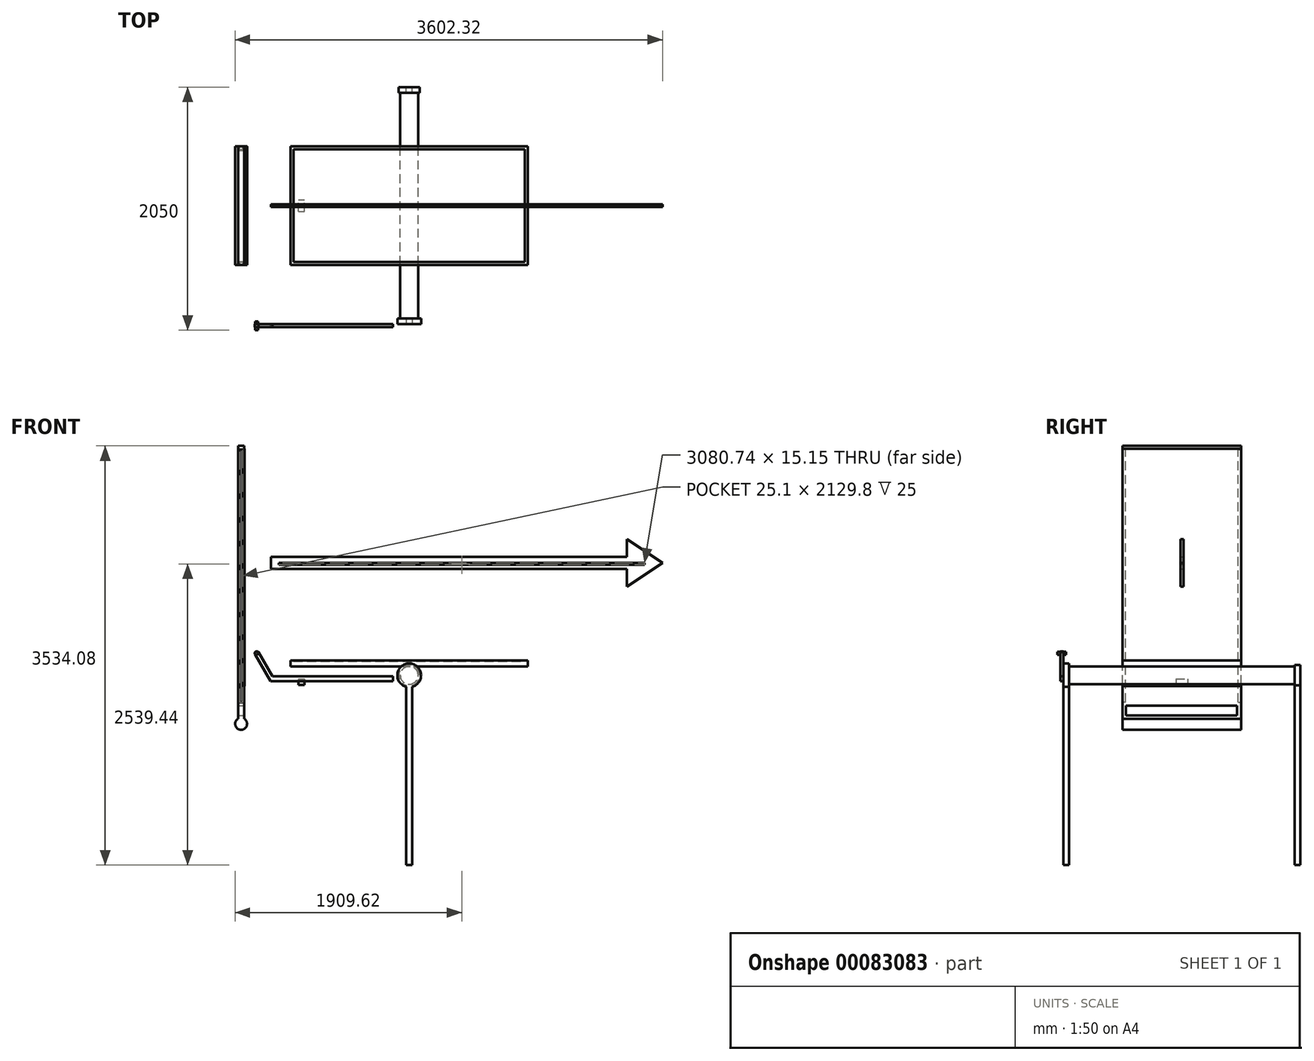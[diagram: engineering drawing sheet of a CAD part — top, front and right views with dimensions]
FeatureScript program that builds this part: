
annotation { "Feature Type Name" : "Feature", "Feature Type Description" : "" }
export const myFeature = defineFeature(function(context is Context, id is Id, definition is map)
    precondition{}
    {
        {
            var Q0;
            Q0=qCreatedBy(makeId("Top.planeOp"),FACE);
            var sketch = newSketch(context, id + "F0", { "sketchPlane" : qUnion([Q0])});
            skLineSegment(sketch, "E0.bottom", {"start": v(-1000, 500) * mm, "end": v(1000, 500) * mm});
            skLineSegment(sketch, "E0.top", {"start": v(-1000, -500) * mm, "end": v(1000, -500) * mm});
            skLineSegment(sketch, "E0.left", {"start": v(-1000, 500) * mm, "end": v(-1000, -500) * mm});
            skLineSegment(sketch, "E0.right", {"start": v(1000, 500) * mm, "end": v(1000, -500) * mm});
            skLineSegment(sketch, "E1", {"start": v(-1000, -500) * mm, "end": v(1000, 500) * mm, "construction": true});
            skSolve(sketch);
        }
        {
            var Q0;
            Q0=makeQuery(id+"F0.imprint","IMPRINT",FACE,{"disambiguationData":[TD([[makeQuery(id+"F0.imprint","IMPRINT",EDGE,{"derivedFrom":sQuery(id+"F0.wireOp",EDGE,"E0.bottom")}),-1.0]])]});
            extrude(context, id + "F1", {"entities" : qUnion([Q0]), "endBound" : BoundingType.SYMMETRIC, "depth" : 50 * mm});
        }
        {
            var Q0;
            Q0=makeQuery(id+"F1.opExtrude","CAP_FACE",FACE,{"disambiguationData":[OSD([sQuery(id+"F0.wireOp",EDGE,"E0.bottom"),sQuery(id+"F0.wireOp",EDGE,"E0.top"),sQuery(id+"F0.wireOp",EDGE,"E0.left"),sQuery(id+"F0.wireOp",EDGE,"E0.right")])],"isStart":false});
            var sketch = newSketch(context, id + "F2", { "sketchPlane" : qUnion([Q0])});
            skLineSegment(sketch, "E2.0", {"start": v(-1000, 500) * mm, "end": v(1000, 500) * mm});
            skLineSegment(sketch, "E3.0", {"start": v(-1000, 500) * mm, "end": v(-1000, -500) * mm});
            skLineSegment(sketch, "E4.0", {"start": v(-1000, -500) * mm, "end": v(1000, -500) * mm});
            skLineSegment(sketch, "E5.0", {"start": v(1000, 500) * mm, "end": v(1000, -500) * mm});
            skLineSegment(sketch, "E6.0", {"start": v(975, 475) * mm, "end": v(975, -475) * mm});
            skLineSegment(sketch, "E6.1", {"start": v(-975, 475) * mm, "end": v(975, 475) * mm});
            skLineSegment(sketch, "E6.2", {"start": v(-975, 475) * mm, "end": v(-975, -475) * mm});
            skLineSegment(sketch, "E6.3", {"start": v(-975, -475) * mm, "end": v(975, -475) * mm});
            skSolve(sketch);
        }
        {
            var Q0;
            Q0=makeQuery(id+"F2.imprint","IMPRINT",FACE,{"disambiguationData":[TD([[makeQuery(id+"F2.imprint","IMPRINT",EDGE,{"derivedFrom":sQuery(id+"F2.wireOp",EDGE,"E2.0")}),-1.0]])]});
            var sketch = newSketch(context, id + "F3", { "sketchPlane" : qUnion([Q0])});
            skSolve(sketch);
        }
        {
            var Q0;
            Q0 = qSketchRegion(id + "F3", true);
            var Q1;
            Q1=makeQuery(id+"F2.imprint","IMPRINT",FACE,{"disambiguationData":[TD([[makeQuery(id+"F2.imprint","IMPRINT",EDGE,{"derivedFrom":sQuery(id+"F2.wireOp",EDGE,"E6.0")}),-1.0]])]});
            extrude(context, id + "F4", {"entities" : qUnion([Q0, Q1]), "operationType" : NewBodyOperationType.REMOVE, "oppositeDirection" : true, "depth" : 5 * mm});
        }
        {
            var Q0;
            Q0=qCreatedBy(makeId("Front.planeOp"),FACE);
            var sketch = newSketch(context, id + "F5", { "sketchPlane" : qUnion([Q0])});
            skCircle(sketch, "E7", {"center": v(0, -100) * mm, "radius": 75 * mm});
            skSolve(sketch);
        }
        {
            var Q0;
            Q0 = qSketchRegion(id + "F5", true);
            extrude(context, id + "F6", {"entities" : qUnion([Q0]), "operationType" : NewBodyOperationType.ADD, "endBound" : BoundingType.SYMMETRIC, "depth" : 2000 * mm});
        }
        {
            var Q0;
            Q0=makeQuery(id+"F6.opExtrude","CAP_FACE",FACE,{"disambiguationData":[OSD([sQuery(id+"F5.wireOp",EDGE,"E7")])],"isStart":false});
            var sketch = newSketch(context, id + "F7", { "sketchPlane" : qUnion([Q0])});
            skCircle(sketch, "E8.0", {"center": v(0, -100) * mm, "radius": 75 * mm});
            skCircle(sketch, "E9", {"center": v(0, -100) * mm, "radius": 100 * mm});
            skSolve(sketch);
        }
        {
            var Q0;
            Q0 = qSketchRegion(id + "F7", true);
            extrude(context, id + "F8", {"entities" : qUnion([Q0]), "operationType" : NewBodyOperationType.ADD, "oppositeDirection" : true, "depth" : 50 * mm});
        }
        {
            var Q0;
            Q0=makeQuery(id+"F8.boolean.opBoolean","MERGE",FACE,{"derivedFrom":[makeQuery(id+"F6.opExtrude","CAP_FACE",FACE,{"disambiguationData":[OSD([sQuery(id+"F5.wireOp",EDGE,"E7")])],"isStart":false}),makeQuery(id+"F8.opExtrude","CAP_FACE",FACE,{"disambiguationData":[OSD([sQuery(id+"F7.wireOp",EDGE,"E8.0"),sQuery(id+"F7.wireOp",EDGE,"E9")])],"isStart":true})]});
            var sketch = newSketch(context, id + "F9", { "sketchPlane" : qUnion([Q0])});
            skLineSegment(sketch, "E10.bottom", {"start": v(-25, -100) * mm, "end": v(25, -100) * mm});
            skLineSegment(sketch, "E10.top", {"start": v(-25, -1700) * mm, "end": v(25, -1700) * mm});
            skLineSegment(sketch, "E10.left", {"start": v(-25, -100) * mm, "end": v(-25, -1700) * mm});
            skLineSegment(sketch, "E10.right", {"start": v(25, -100) * mm, "end": v(25, -1700) * mm});
            skPoint(sketch, "E11", {"position": v(0, -100) * mm});
            skSolve(sketch);
        }
        {
            var Q0;
            Q0 = qSketchRegion(id + "F9", true);
            extrude(context, id + "F10", {"entities" : qUnion([Q0]), "operationType" : NewBodyOperationType.ADD, "oppositeDirection" : true, "depth" : 50 * mm});
        }
        {
            var Q0;
            Q0=makeQuery(id+"F6.opExtrude","CAP_FACE",FACE,{"disambiguationData":[OSD([sQuery(id+"F5.wireOp",EDGE,"E7")])],"isStart":true});
            var sketch = newSketch(context, id + "F11", { "sketchPlane" : qUnion([Q0])});
            skCircle(sketch, "E12", {"center": v(0, -100) * mm, "radius": 87.5 * mm});
            skCircle(sketch, "E13.0", {"center": v(0, -100) * mm, "radius": 75 * mm});
            skSolve(sketch);
        }
        {
            var Q0;
            Q0 = qSketchRegion(id + "F11", true);
            extrude(context, id + "F12", {"entities" : qUnion([Q0]), "operationType" : NewBodyOperationType.ADD, "oppositeDirection" : true, "depth" : 50 * mm});
        }
        {
            var Q0;
            Q0=makeQuery(id+"F12.boolean.opBoolean","MERGE",FACE,{"derivedFrom":[makeQuery(id+"F6.opExtrude","CAP_FACE",FACE,{"disambiguationData":[OSD([sQuery(id+"F5.wireOp",EDGE,"E7")])],"isStart":true}),makeQuery(id+"F12.opExtrude","CAP_FACE",FACE,{"disambiguationData":[OSD([sQuery(id+"F11.wireOp",EDGE,"E12"),sQuery(id+"F11.wireOp",EDGE,"E13.0")])],"isStart":true})]});
            var sketch = newSketch(context, id + "F13", { "sketchPlane" : qUnion([Q0])});
            skLineSegment(sketch, "E14.0", {"start": v(25, -100) * mm, "end": v(-25, -100) * mm});
            skLineSegment(sketch, "E14.1", {"start": v(25, -1700) * mm, "end": v(-25, -1700) * mm});
            skLineSegment(sketch, "E14.2", {"start": v(25, -100) * mm, "end": v(25, -1700) * mm});
            skLineSegment(sketch, "E14.3", {"start": v(-25, -100) * mm, "end": v(-25, -1700) * mm});
            skPoint(sketch, "E14.4", {"position": v(0, -100) * mm});
            skSolve(sketch);
        }
        {
            var Q0;
            Q0 = qSketchRegion(id + "F13", true);
            extrude(context, id + "F14", {"entities" : qUnion([Q0]), "operationType" : NewBodyOperationType.ADD, "oppositeDirection" : true, "depth" : 50 * mm});
        }
        {
            var Q0;
            Q0=qCreatedBy(makeId("Front.planeOp"),FACE);
            var sketch = newSketch(context, id + "F15", { "sketchPlane" : qUnion([Q0])});
            skArc(sketch, "E15", {"start": v(-1441.7, -465.92) * mm, "mid": v(-1416.7, -559.22) * mm, "end": v(-1391.7, -465.92) * mm});
            skLineSegment(sketch, "E16.top", {"start": v(-1441.7, 1834.08) * mm, "end": v(-1391.7, 1834.08) * mm});
            skLineSegment(sketch, "E16.left", {"start": v(-1441.7, -465.92) * mm, "end": v(-1441.7, 1834.08) * mm});
            skLineSegment(sketch, "E16.right", {"start": v(-1391.7, -465.92) * mm, "end": v(-1391.7, 1834.08) * mm});
            skSolve(sketch);
        }
        {
            var Q0;
            Q0 = qSketchRegion(id + "F15", true);
            extrude(context, id + "F16", {"entities" : qUnion([Q0]), "endBound" : BoundingType.SYMMETRIC, "depth" : 1000 * mm});
        }
        {
            var Q0;
            Q0=makeQuery(id+"F16.opExtrude","CAP_FACE",FACE,{"disambiguationData":[OSD([sQuery(id+"F15.wireOp",EDGE,"E15"),sQuery(id+"F15.wireOp",EDGE,"E16.top"),sQuery(id+"F15.wireOp",EDGE,"E16.left"),sQuery(id+"F15.wireOp",EDGE,"E16.right")])],"isStart":false});
            var sketch = newSketch(context, id + "F17", { "sketchPlane" : qUnion([Q0])});
            skLineSegment(sketch, "E17.bottom", {"start": v(-1429.3, -326.34) * mm, "end": v(-1404.2, -326.34) * mm});
            skLineSegment(sketch, "E17.left", {"start": v(-1429.3, -326.34) * mm, "end": v(-1429.3, 1803.46) * mm});
            skLineSegment(sketch, "E17.right", {"start": v(-1404.2, -326.34) * mm, "end": v(-1404.2, 1803.46) * mm});
            skLineSegment(sketch, "E18", {"start": v(-1429.3, 1803.46) * mm, "end": v(-1404.2, 1803.46) * mm});
            skSolve(sketch);
        }
        {
            var Q0;
            Q0 = qSketchRegion(id + "F17", true);
            extrude(context, id + "F18", {"entities" : qUnion([Q0]), "operationType" : NewBodyOperationType.REMOVE, "oppositeDirection" : true, "depth" : 25 * mm});
        }
        {
            var Q0;
            Q0=makeQuery(id+"F16.opExtrude","SWEPT_BODY",BODY,{"disambiguationData":[OSD([sQuery(id+"F15.wireOp",EDGE,"E15"),sQuery(id+"F15.wireOp",EDGE,"E16.top"),sQuery(id+"F15.wireOp",EDGE,"E16.left"),sQuery(id+"F15.wireOp",EDGE,"E16.right")])]});
            var Q1;
            Q1=makeQuery(id+"F18.boolean.opBoolean","COPY",FACE,{"derivedFrom":makeQuery(id+"F18.opExtrude","SWEPT_FACE",FACE,{"disambiguationData":[OSD([sQuery(id+"F17.wireOp",EDGE,"E17.bottom")])]})});
            var Q2;
            Q2=makeQuery(id+"F18.boolean.opBoolean","COPY",FACE,{"derivedFrom":makeQuery(id+"F18.opExtrude","CAP_FACE",FACE,{"disambiguationData":[OSD([sQuery(id+"F17.wireOp",EDGE,"E17.bottom"),sQuery(id+"F17.wireOp",EDGE,"E17.left"),sQuery(id+"F17.wireOp",EDGE,"E17.right"),sQuery(id+"F17.wireOp",EDGE,"E18")])],"isStart":false})});
            var Q3;
            Q3=makeQuery(id+"F18.boolean.opBoolean","COPY",FACE,{"derivedFrom":makeQuery(id+"F18.opExtrude","SWEPT_FACE",FACE,{"disambiguationData":[OSD([sQuery(id+"F17.wireOp",EDGE,"E17.left")])]})});
            var Q4;
            Q4=makeQuery(id+"F18.boolean.opBoolean","COPY",FACE,{"derivedFrom":makeQuery(id+"F18.opExtrude","SWEPT_FACE",FACE,{"disambiguationData":[OSD([sQuery(id+"F17.wireOp",EDGE,"E17.right")])]})});
            var Q5;
            Q5=makeQuery(id+"F18.boolean.opBoolean","COPY",FACE,{"derivedFrom":makeQuery(id+"F18.opExtrude","SWEPT_FACE",FACE,{"disambiguationData":[OSD([sQuery(id+"F17.wireOp",EDGE,"E18")])]})});
            var Q6;
            Q6=qCreatedBy(makeId("Front.planeOp"),FACE);
            mirror(context, id + "F19", {"entities" : qUnion([Q0]), "faces" : qUnion([Q1, Q2, Q3, Q4, Q5]), "mirrorPlane" : qUnion([Q6]), "patternType" : MirrorType.FACE});
        }
        {
            var Q0;
            Q0=makeQuery(id+"F16.opExtrude","SWEPT_FACE",FACE,{"disambiguationData":[OSD([sQuery(id+"F15.wireOp",EDGE,"E16.right")])]});
            var sketch = newSketch(context, id + "F20", { "sketchPlane" : qUnion([Q0])});
            skLineSegment(sketch, "E19.bottom", {"start": v(-470.62, -438.51) * mm, "end": v(465.7, -438.51) * mm});
            skLineSegment(sketch, "E19.top", {"start": v(-470.62, -355.39) * mm, "end": v(465.7, -355.39) * mm});
            skLineSegment(sketch, "E19.left", {"start": v(-470.62, -438.51) * mm, "end": v(-470.62, -355.39) * mm});
            skLineSegment(sketch, "E19.right", {"start": v(465.7, -438.51) * mm, "end": v(465.7, -355.39) * mm});
            skSolve(sketch);
        }
        {
            var Q0;
            Q0 = qSketchRegion(id + "F20", true);
            extrude(context, id + "F21", {"entities" : qUnion([Q0]), "operationType" : NewBodyOperationType.REMOVE, "endBound" : BoundingType.THROUGH_ALL, "oppositeDirection" : true, "depth" : 25 * mm});
        }
        {
            var Q0;
            Q0=makeQuery(id+"F16.opExtrude","SWEPT_FACE",FACE,{"disambiguationData":[OSD([sQuery(id+"F15.wireOp",EDGE,"E16.right")])]});
            var sketch = newSketch(context, id + "F22", { "sketchPlane" : qUnion([Q0])});
            skLineSegment(sketch, "E20.bottom", {"start": v(-500, 1809.08) * mm, "end": v(500, 1809.08) * mm});
            skLineSegment(sketch, "E20.top", {"start": v(-500, -190.92) * mm, "end": v(500, -190.92) * mm});
            skLineSegment(sketch, "E20.left", {"start": v(-500, 1809.08) * mm, "end": v(-500, -190.92) * mm});
            skLineSegment(sketch, "E20.right", {"start": v(500, 1809.08) * mm, "end": v(500, -190.92) * mm});
            skSolve(sketch);
        }
        {
            var Q0;
            Q0 = qSketchRegion(id + "F22", true);
            extrude(context, id + "F23", {"entities" : qUnion([Q0]), "operationType" : NewBodyOperationType.ADD, "depth" : 4 * mm});
        }
        {
            var Q0;
            Q0=makeQuery(id+"F7.imprint","IMPRINT",FACE,{"disambiguationData":[TD([[makeQuery(id+"F7.imprint","IMPRINT",EDGE,{"derivedFrom":sQuery(id+"F7.wireOp",EDGE,"E8.0")}),1.0]])]});
            var sketch = newSketch(context, id + "F24", { "sketchPlane" : qUnion([Q0])});
            skLineSegment(sketch, "E21", {"start": v(-136.39, -109.44) * mm, "end": v(-1152.42, -109.44) * mm});
            skLineSegment(sketch, "E22", {"start": v(-1152.42, -109.44) * mm, "end": v(-1270.64, 95.33) * mm});
            skLineSegment(sketch, "E23", {"start": v(-1300.02, 76.23) * mm, "end": v(-1169.74, -149.44) * mm});
            skLineSegment(sketch, "E24", {"start": v(-1169.74, -149.44) * mm, "end": v(-136.39, -149.44) * mm});
            skLineSegment(sketch, "E25", {"start": v(-136.39, -109.44) * mm, "end": v(-136.39, -149.44) * mm});
            skCircle(sketch, "E26", {"center": v(-1284.83, 85) * mm, "radius": 12.5 * mm});
            skArc(sketch, "E27", {"start": v(-1270.64, 95.33) * mm, "mid": v(-1294.4, 99.71) * mm, "end": v(-1300.02, 76.23) * mm});
            skSolve(sketch);
        }
        {
            var Q0;
            Q0 = qSketchRegion(id + "F24", true);
            var Q1;
            Q1 = qSketchRegion(id + "F26", true);
            extrude(context, id + "F25", {"entities" : qUnion([Q0, Q1]), "depth" : 25 * mm});
        }
        {
            var Q0;
            Q0=makeQuery(id+"F25.opExtrude","CAP_FACE",FACE,{"disambiguationData":[OSD([sQuery(id+"F24.wireOp",EDGE,"E21"),sQuery(id+"F24.wireOp",EDGE,"E22"),sQuery(id+"F24.wireOp",EDGE,"E23"),sQuery(id+"F24.wireOp",EDGE,"E24"),sQuery(id+"F24.wireOp",EDGE,"E25"),sQuery(id+"F24.wireOp",EDGE,"E26"),sQuery(id+"F24.wireOp",EDGE,"E27")])],"isStart":false});
            var sketch = newSketch(context, id + "F26", { "sketchPlane" : qUnion([Q0])});
            skCircle(sketch, "E28.0", {"center": v(-1284.83, 85) * mm, "radius": 12.5 * mm});
            skSolve(sketch);
        }
        {
            var Q0;
            Q0 = qSketchRegion(id + "F26", true);
            extrude(context, id + "F27", {"entities" : qUnion([Q0]), "operationType" : NewBodyOperationType.ADD, "oppositeDirection" : true, "depth" : 50 * mm, "hasSecondDirection" : true, "secondDirectionOppositeDirection" : false, "secondDirectionDepth" : 25 * mm});
        }
        {
            var Q0;
            Q0=qCreatedBy(makeId("Front.planeOp"),FACE);
            var sketch = newSketch(context, id + "F28", { "sketchPlane" : qUnion([Q0])});
            skLineSegment(sketch, "E29", {"start": v(-1164.4, 797.02) * mm, "end": v(1835.6, 797.02) * mm});
            skLineSegment(sketch, "E30", {"start": v(1835.6, 797.02) * mm, "end": v(1835.6, 647.02) * mm});
            skLineSegment(sketch, "E31", {"start": v(1835.6, 647.02) * mm, "end": v(2135.6, 847.02) * mm});
            skLineSegment(sketch, "E32", {"start": v(2135.6, 847.02) * mm, "end": v(1835.6, 1047.02) * mm});
            skLineSegment(sketch, "E33", {"start": v(1835.6, 1047.02) * mm, "end": v(1835.6, 897.02) * mm});
            skLineSegment(sketch, "E34", {"start": v(1835.6, 897.02) * mm, "end": v(-1164.4, 897.02) * mm});
            skLineSegment(sketch, "E35", {"start": v(-1164.4, 897.02) * mm, "end": v(-1164.4, 797.02) * mm});
            skSolve(sketch);
        }
        {
            var Q0;
            Q0 = qSketchRegion(id + "F28", true);
            extrude(context, id + "F29", {"entities" : qUnion([Q0]), "operationType" : NewBodyOperationType.ADD, "endBound" : BoundingType.SYMMETRIC, "depth" : 25 * mm});
        }
        {
            var Q0;
            Q0=makeQuery(id+"F29.opExtrude","CAP_EDGE",EDGE,{"disambiguationData":[OSD([sQuery(id+"F28.wireOp",EDGE,"E35")])],"isStart":false});
            cPlane(context, id + "F30", {"entities" : qUnion([Q0]), "cplaneType" : CPlaneType.MID_PLANE, "offset" : 150 * mm, "width" : 150 * mm, "height" : 150 * mm});
        }
        {
            var Q0;
            Q0=makeQuery(id+"F29.opExtrude","CAP_FACE",FACE,{"disambiguationData":[OSD([sQuery(id+"F28.wireOp",EDGE,"E29"),sQuery(id+"F28.wireOp",EDGE,"E30"),sQuery(id+"F28.wireOp",EDGE,"E31"),sQuery(id+"F28.wireOp",EDGE,"E32"),sQuery(id+"F28.wireOp",EDGE,"E33"),sQuery(id+"F28.wireOp",EDGE,"E34"),sQuery(id+"F28.wireOp",EDGE,"E35")])],"isStart":false});
            var sketch = newSketch(context, id + "F31", { "sketchPlane" : qUnion([Q0])});
            skLineSegment(sketch, "E36.bottom", {"start": v(1983.28, 847.02) * mm, "end": v(-1097.46, 847.02) * mm});
            skLineSegment(sketch, "E36.top", {"start": v(1983.28, 831.87) * mm, "end": v(-1097.46, 831.87) * mm});
            skLineSegment(sketch, "E36.left", {"start": v(1983.28, 847.02) * mm, "end": v(1983.28, 831.87) * mm});
            skLineSegment(sketch, "E36.right", {"start": v(-1097.46, 847.02) * mm, "end": v(-1097.46, 831.87) * mm});
            skSolve(sketch);
        }
        {
            var Q0;
            Q0 = qSketchRegion(id + "F31", true);
            extrude(context, id + "F32", {"entities" : qUnion([Q0]), "operationType" : NewBodyOperationType.REMOVE, "endBound" : BoundingType.THROUGH_ALL, "oppositeDirection" : true, "depth" : 25 * mm});
        }
        {
            var Q0;
            Q0=qCreatedBy(makeId("Front.planeOp"),FACE);
            var sketch = newSketch(context, id + "F33", { "sketchPlane" : qUnion([Q0])});
            skCircle(sketch, "E37", {"center": v(-900.5, 269.22) * mm, "radius": 25 * mm});
            skSolve(sketch);
        }
        {
            var Q0;
            Q0 = qSketchRegion(id + "F33", true);
            extrude(context, id + "F34", {"entities" : qUnion([Q0]), "endBound" : BoundingType.SYMMETRIC, "depth" : 100 * mm});
        }
        {
            var Q0;
            Q0=qCreatedBy(makeId("Front.planeOp"),FACE);
            var sketch = newSketch(context, id + "F35", { "sketchPlane" : qUnion([Q0])});
            skLineSegment(sketch, "E38.bottom", {"start": v(-932.76, -131.48) * mm, "end": v(-882.76, -131.48) * mm});
            skLineSegment(sketch, "E38.top", {"start": v(-932.76, -181.48) * mm, "end": v(-882.76, -181.48) * mm});
            skLineSegment(sketch, "E38.left", {"start": v(-932.76, -131.48) * mm, "end": v(-932.76, -181.48) * mm});
            skLineSegment(sketch, "E38.right", {"start": v(-882.76, -131.48) * mm, "end": v(-882.76, -181.48) * mm});
            skSolve(sketch);
        }
        {
            var Q0;
            Q0 = qSketchRegion(id + "F35", true);
            extrude(context, id + "F36", {"entities" : qUnion([Q0]), "endBound" : BoundingType.SYMMETRIC, "depth" : 100 * mm});
        }
        {
            var Q0;
            Q0=makeQuery(id+"F34.opExtrude","SWEPT_BODY",BODY,{"disambiguationData":[OSD([sQuery(id+"F33.wireOp",EDGE,"E37")])]});
            deleteBodies(context, id + "F37", {"entities" : qUnion([Q0])});
        }
    });
